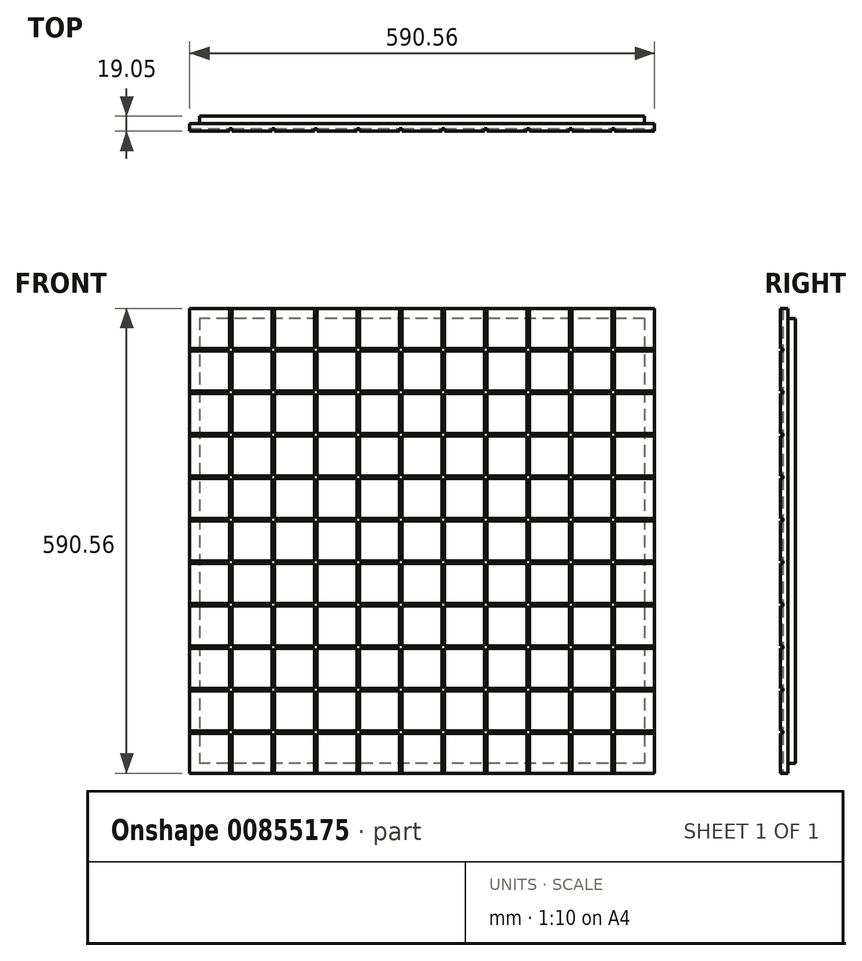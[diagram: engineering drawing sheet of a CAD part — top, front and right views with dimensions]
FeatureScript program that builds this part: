
annotation { "Feature Type Name" : "Feature", "Feature Type Description" : "" }
export const myFeature = defineFeature(function(context is Context, id is Id, definition is map)
    precondition{}
    {
        {
            var Q0;
            Q0=qCreatedBy(makeId("Front.planeOp"),FACE);
            var sketch = newSketch(context, id + "F0", { "sketchPlane" : qUnion([Q0])});
            skLineSegment(sketch, "E0.bottom", {"start": v(295.27, 295.28) * mm, "end": v(-295.27, 295.28) * mm});
            skLineSegment(sketch, "E0.top", {"start": v(295.27, -295.28) * mm, "end": v(-295.27, -295.28) * mm});
            skLineSegment(sketch, "E0.left", {"start": v(295.28, 295.27) * mm, "end": v(295.28, -295.28) * mm});
            skLineSegment(sketch, "E0.right", {"start": v(-295.28, 295.27) * mm, "end": v(-295.28, -295.27) * mm});
            skPoint(sketch, "E0.middle", {"position": v(0, 0) * mm});
            skSolve(sketch);
        }
        {
            var Q0;
            Q0=makeQuery(id+"F0.imprint","IMPRINT",FACE,{"disambiguationData":[TD([[makeQuery(id+"F0.imprint","IMPRINT",EDGE,{"derivedFrom":sQuery(id+"F0.wireOp",EDGE,"E0.bottom")}),1.0]])]});
            extrude(context, id + "F1", {"entities" : qUnion([Q0]), "depth" : 19.05 * mm, "offsetDistance" : 25.4 * mm});
        }
        {
            var Q0;
            Q0=makeQuery(id+"F1.opExtrude","CAP_FACE",FACE,{"disambiguationData":[OSD([sQuery(id+"F0.wireOp",EDGE,"E0.bottom"),sQuery(id+"F0.wireOp",EDGE,"E0.top"),sQuery(id+"F0.wireOp",EDGE,"E0.left"),sQuery(id+"F0.wireOp",EDGE,"E0.right")])],"isStart":false});
            var sketch = newSketch(context, id + "F2", { "sketchPlane" : qUnion([Q0])});
            skLineSegment(sketch, "E1.bottom", {"start": v(-244.48, 295.28) * mm, "end": v(-241.3, 295.28) * mm});
            skLineSegment(sketch, "E1.top", {"start": v(-244.47, -295.28) * mm, "end": v(-241.3, -295.28) * mm});
            skLineSegment(sketch, "E1.left", {"start": v(-244.48, 295.28) * mm, "end": v(-244.47, -295.28) * mm});
            skLineSegment(sketch, "E1.right", {"start": v(-241.3, 295.28) * mm, "end": v(-241.3, -295.28) * mm});
            skLineSegment(sketch, "E2.1.0.0", {"start": v(-190.5, 295.28) * mm, "end": v(-190.5, -295.28) * mm});
            skLineSegment(sketch, "E2.1.0.1", {"start": v(-187.32, 295.28) * mm, "end": v(-187.32, -295.28) * mm});
            skLineSegment(sketch, "E2.1.0.2", {"start": v(-190.5, 295.28) * mm, "end": v(-187.32, 295.28) * mm});
            skLineSegment(sketch, "E2.2.0.0", {"start": v(-136.52, 295.28) * mm, "end": v(-136.53, -295.28) * mm});
            skLineSegment(sketch, "E2.2.0.1", {"start": v(-133.35, 295.28) * mm, "end": v(-133.35, -295.28) * mm});
            skLineSegment(sketch, "E2.2.0.2", {"start": v(-136.52, 295.28) * mm, "end": v(-133.35, 295.28) * mm});
            skLineSegment(sketch, "E2.direction1", {"start": v(-244.47, -295.28) * mm, "end": v(-190.5, -295.28) * mm, "construction": true});
            skLineSegment(sketch, "E3.1.0.0", {"start": v(-190.5, -295.28) * mm, "end": v(-187.32, -295.28) * mm});
            skLineSegment(sketch, "E3.2.0.0", {"start": v(-136.52, -295.28) * mm, "end": v(-133.35, -295.28) * mm});
            skLineSegment(sketch, "E4.0.3.0", {"start": v(-82.55, -295.28) * mm, "end": v(-79.38, -295.28) * mm});
            skLineSegment(sketch, "E4.0.4.0", {"start": v(-28.57, -295.28) * mm, "end": v(-25.4, -295.28) * mm});
            skLineSegment(sketch, "E4.0.5.0", {"start": v(25.4, -295.28) * mm, "end": v(28.57, -295.28) * mm});
            skLineSegment(sketch, "E4.0.6.0", {"start": v(79.38, -295.28) * mm, "end": v(82.55, -295.28) * mm});
            skLineSegment(sketch, "E4.0.7.0", {"start": v(133.35, -295.28) * mm, "end": v(136.52, -295.28) * mm});
            skLineSegment(sketch, "E4.0.8.0", {"start": v(187.32, -295.28) * mm, "end": v(190.5, -295.28) * mm});
            skLineSegment(sketch, "E4.0.9.0", {"start": v(241.3, -295.28) * mm, "end": v(244.47, -295.28) * mm});
            skLineSegment(sketch, "E5.0.3.0", {"start": v(-82.55, 295.28) * mm, "end": v(-82.55, -295.28) * mm});
            skLineSegment(sketch, "E5.3.3.0", {"start": v(-79.37, 295.28) * mm, "end": v(-79.37, -295.28) * mm});
            skLineSegment(sketch, "E5.6.3.0", {"start": v(-82.55, 295.28) * mm, "end": v(-79.37, 295.28) * mm});
            skLineSegment(sketch, "E5.0.4.0", {"start": v(-28.57, 295.28) * mm, "end": v(-28.57, -295.28) * mm});
            skLineSegment(sketch, "E5.3.4.0", {"start": v(-25.4, 295.28) * mm, "end": v(-25.4, -295.28) * mm});
            skLineSegment(sketch, "E5.6.4.0", {"start": v(-28.57, 295.28) * mm, "end": v(-25.4, 295.28) * mm});
            skLineSegment(sketch, "E5.0.5.0", {"start": v(25.4, 295.28) * mm, "end": v(25.4, -295.28) * mm});
            skLineSegment(sketch, "E5.3.5.0", {"start": v(28.58, 295.28) * mm, "end": v(28.58, -295.28) * mm});
            skLineSegment(sketch, "E5.6.5.0", {"start": v(25.4, 295.28) * mm, "end": v(28.58, 295.28) * mm});
            skLineSegment(sketch, "E5.0.6.0", {"start": v(79.38, 295.28) * mm, "end": v(79.38, -295.28) * mm});
            skLineSegment(sketch, "E5.3.6.0", {"start": v(82.55, 295.28) * mm, "end": v(82.55, -295.28) * mm});
            skLineSegment(sketch, "E5.6.6.0", {"start": v(79.38, 295.28) * mm, "end": v(82.55, 295.28) * mm});
            skLineSegment(sketch, "E5.0.7.0", {"start": v(133.35, 295.28) * mm, "end": v(133.35, -295.28) * mm});
            skLineSegment(sketch, "E5.3.7.0", {"start": v(136.53, 295.28) * mm, "end": v(136.53, -295.28) * mm});
            skLineSegment(sketch, "E5.6.7.0", {"start": v(133.35, 295.28) * mm, "end": v(136.53, 295.28) * mm});
            skLineSegment(sketch, "E5.0.8.0", {"start": v(187.33, 295.28) * mm, "end": v(187.33, -295.28) * mm});
            skLineSegment(sketch, "E5.3.8.0", {"start": v(190.5, 295.28) * mm, "end": v(190.5, -295.28) * mm});
            skLineSegment(sketch, "E5.6.8.0", {"start": v(187.33, 295.28) * mm, "end": v(190.5, 295.28) * mm});
            skLineSegment(sketch, "E5.0.9.0", {"start": v(241.3, 295.28) * mm, "end": v(241.3, -295.28) * mm});
            skLineSegment(sketch, "E5.3.9.0", {"start": v(244.48, 295.28) * mm, "end": v(244.48, -295.28) * mm});
            skLineSegment(sketch, "E5.6.9.0", {"start": v(241.3, 295.28) * mm, "end": v(244.48, 295.28) * mm});
            skSolve(sketch);
        }
        {
            var Q0;
            Q0 = qSketchRegion(id + "F2", true);
            extrude(context, id + "F3", {"entities" : qUnion([Q0]), "operationType" : NewBodyOperationType.REMOVE, "oppositeDirection" : true, "depth" : 3.17 * mm, "offsetDistance" : 25.4 * mm});
        }
        {
            var Q0;
            {var subQ0=sQuery(id+"F0.wireOp",EDGE,"E0.bottom");var subQ1=sQuery(id+"F0.wireOp",EDGE,"E0.right");var subQ2=sQuery(id+"F0.wireOp",EDGE,"E0.top");Q0=makeQuery(id+"F3.boolean.opBoolean","SPLIT",FACE,{"disambiguationData":[TD([makeQuery(id+"F1.opExtrude","SWEPT_FACE",FACE,{"disambiguationData":[OSD([subQ1])]})])],"derivedFrom":makeQuery(id+"F1.opExtrude","CAP_FACE",FACE,{"disambiguationData":[OSD([subQ0,subQ2,sQuery(id+"F0.wireOp",EDGE,"E0.left"),subQ1])],"isStart":false})});}
            var sketch = newSketch(context, id + "F4", { "sketchPlane" : qUnion([Q0])});
            skLineSegment(sketch, "E6.bottom", {"start": v(-295.27, 244.47) * mm, "end": v(295.28, 244.47) * mm});
            skLineSegment(sketch, "E6.top", {"start": v(-295.27, 241.3) * mm, "end": v(295.28, 241.3) * mm});
            skLineSegment(sketch, "E6.left", {"start": v(-295.28, 244.47) * mm, "end": v(-295.28, 241.3) * mm});
            skLineSegment(sketch, "E6.right", {"start": v(295.28, 244.47) * mm, "end": v(295.28, 241.3) * mm});
            skLineSegment(sketch, "E7.0.1.0", {"start": v(-295.28, 190.5) * mm, "end": v(-295.28, 187.33) * mm});
            skLineSegment(sketch, "E7.0.1.1", {"start": v(-295.27, 190.5) * mm, "end": v(295.28, 190.5) * mm});
            skLineSegment(sketch, "E7.0.1.2", {"start": v(-295.27, 187.32) * mm, "end": v(295.28, 187.32) * mm});
            skLineSegment(sketch, "E7.0.1.3", {"start": v(295.28, 190.5) * mm, "end": v(295.28, 187.32) * mm});
            skLineSegment(sketch, "E7.0.2.0", {"start": v(-295.28, 136.53) * mm, "end": v(-295.28, 133.35) * mm});
            skLineSegment(sketch, "E7.0.2.1", {"start": v(-295.27, 136.53) * mm, "end": v(295.28, 136.53) * mm});
            skLineSegment(sketch, "E7.0.2.2", {"start": v(-295.27, 133.35) * mm, "end": v(295.28, 133.35) * mm});
            skLineSegment(sketch, "E7.0.2.3", {"start": v(295.28, 136.53) * mm, "end": v(295.28, 133.35) * mm});
            skLineSegment(sketch, "E7.0.3.0", {"start": v(-295.28, 82.55) * mm, "end": v(-295.28, 79.38) * mm});
            skLineSegment(sketch, "E7.0.3.1", {"start": v(-295.27, 82.55) * mm, "end": v(295.28, 82.55) * mm});
            skLineSegment(sketch, "E7.0.3.2", {"start": v(-295.27, 79.38) * mm, "end": v(295.28, 79.38) * mm});
            skLineSegment(sketch, "E7.0.3.3", {"start": v(295.28, 82.55) * mm, "end": v(295.28, 79.38) * mm});
            skLineSegment(sketch, "E7.0.4.0", {"start": v(-295.28, 28.58) * mm, "end": v(-295.28, 25.4) * mm});
            skLineSegment(sketch, "E7.0.4.1", {"start": v(-295.27, 28.58) * mm, "end": v(295.28, 28.58) * mm});
            skLineSegment(sketch, "E7.0.4.2", {"start": v(-295.27, 25.4) * mm, "end": v(295.28, 25.4) * mm});
            skLineSegment(sketch, "E7.0.4.3", {"start": v(295.28, 28.58) * mm, "end": v(295.28, 25.4) * mm});
            skLineSegment(sketch, "E7.0.5.0", {"start": v(-295.28, -25.4) * mm, "end": v(-295.28, -28.57) * mm});
            skLineSegment(sketch, "E7.0.5.1", {"start": v(-295.27, -25.4) * mm, "end": v(295.28, -25.4) * mm});
            skLineSegment(sketch, "E7.0.5.2", {"start": v(-295.27, -28.57) * mm, "end": v(295.28, -28.57) * mm});
            skLineSegment(sketch, "E7.0.5.3", {"start": v(295.28, -25.4) * mm, "end": v(295.28, -28.57) * mm});
            skLineSegment(sketch, "E7.0.6.0", {"start": v(-295.28, -79.37) * mm, "end": v(-295.28, -82.55) * mm});
            skLineSegment(sketch, "E7.0.6.1", {"start": v(-295.27, -79.37) * mm, "end": v(295.28, -79.37) * mm});
            skLineSegment(sketch, "E7.0.6.2", {"start": v(-295.27, -82.55) * mm, "end": v(295.28, -82.55) * mm});
            skLineSegment(sketch, "E7.0.6.3", {"start": v(295.28, -79.37) * mm, "end": v(295.28, -82.55) * mm});
            skLineSegment(sketch, "E7.0.7.0", {"start": v(-295.28, -133.35) * mm, "end": v(-295.28, -136.52) * mm});
            skLineSegment(sketch, "E7.0.7.1", {"start": v(-295.27, -133.35) * mm, "end": v(295.28, -133.35) * mm});
            skLineSegment(sketch, "E7.0.7.2", {"start": v(-295.27, -136.52) * mm, "end": v(295.28, -136.52) * mm});
            skLineSegment(sketch, "E7.0.7.3", {"start": v(295.28, -133.35) * mm, "end": v(295.28, -136.52) * mm});
            skLineSegment(sketch, "E7.0.8.0", {"start": v(-295.28, -187.32) * mm, "end": v(-295.28, -190.5) * mm});
            skLineSegment(sketch, "E7.0.8.1", {"start": v(-295.27, -187.32) * mm, "end": v(295.28, -187.32) * mm});
            skLineSegment(sketch, "E7.0.8.2", {"start": v(-295.27, -190.5) * mm, "end": v(295.28, -190.5) * mm});
            skLineSegment(sketch, "E7.0.8.3", {"start": v(295.28, -187.32) * mm, "end": v(295.28, -190.5) * mm});
            skLineSegment(sketch, "E7.0.9.0", {"start": v(-295.28, -241.3) * mm, "end": v(-295.28, -244.47) * mm});
            skLineSegment(sketch, "E7.0.9.1", {"start": v(-295.27, -241.3) * mm, "end": v(295.28, -241.3) * mm});
            skLineSegment(sketch, "E7.0.9.2", {"start": v(-295.27, -244.47) * mm, "end": v(295.28, -244.47) * mm});
            skLineSegment(sketch, "E7.0.9.3", {"start": v(295.28, -241.3) * mm, "end": v(295.28, -244.47) * mm});
            skLineSegment(sketch, "E7.1.1.0", {"start": v(-295.28, 190.5) * mm, "end": v(-295.28, 187.33) * mm});
            skLineSegment(sketch, "E7.1.1.1", {"start": v(-295.27, 190.5) * mm, "end": v(295.28, 190.5) * mm});
            skLineSegment(sketch, "E7.1.1.2", {"start": v(-295.27, 187.32) * mm, "end": v(295.28, 187.32) * mm});
            skLineSegment(sketch, "E7.1.1.3", {"start": v(295.28, 190.5) * mm, "end": v(295.28, 187.32) * mm});
            skLineSegment(sketch, "E7.1.2.0", {"start": v(-295.28, 136.53) * mm, "end": v(-295.28, 133.35) * mm});
            skLineSegment(sketch, "E7.1.2.1", {"start": v(-295.27, 136.53) * mm, "end": v(295.28, 136.53) * mm});
            skLineSegment(sketch, "E7.1.2.2", {"start": v(-295.27, 133.35) * mm, "end": v(295.28, 133.35) * mm});
            skLineSegment(sketch, "E7.1.2.3", {"start": v(295.28, 136.53) * mm, "end": v(295.28, 133.35) * mm});
            skLineSegment(sketch, "E7.1.3.0", {"start": v(-295.28, 82.55) * mm, "end": v(-295.28, 79.38) * mm});
            skLineSegment(sketch, "E7.1.3.1", {"start": v(-295.27, 82.55) * mm, "end": v(295.28, 82.55) * mm});
            skLineSegment(sketch, "E7.1.3.2", {"start": v(-295.27, 79.38) * mm, "end": v(295.28, 79.38) * mm});
            skLineSegment(sketch, "E7.1.3.3", {"start": v(295.28, 82.55) * mm, "end": v(295.28, 79.38) * mm});
            skLineSegment(sketch, "E7.1.4.0", {"start": v(-295.28, 28.58) * mm, "end": v(-295.28, 25.4) * mm});
            skLineSegment(sketch, "E7.1.4.1", {"start": v(-295.27, 28.58) * mm, "end": v(295.28, 28.58) * mm});
            skLineSegment(sketch, "E7.1.4.2", {"start": v(-295.27, 25.4) * mm, "end": v(295.28, 25.4) * mm});
            skLineSegment(sketch, "E7.1.4.3", {"start": v(295.28, 28.58) * mm, "end": v(295.28, 25.4) * mm});
            skLineSegment(sketch, "E7.1.5.0", {"start": v(-295.28, -25.4) * mm, "end": v(-295.28, -28.57) * mm});
            skLineSegment(sketch, "E7.1.5.1", {"start": v(-295.27, -25.4) * mm, "end": v(295.28, -25.4) * mm});
            skLineSegment(sketch, "E7.1.5.2", {"start": v(-295.27, -28.57) * mm, "end": v(295.28, -28.57) * mm});
            skLineSegment(sketch, "E7.1.5.3", {"start": v(295.28, -25.4) * mm, "end": v(295.28, -28.57) * mm});
            skLineSegment(sketch, "E7.1.6.0", {"start": v(-295.28, -79.37) * mm, "end": v(-295.28, -82.55) * mm});
            skLineSegment(sketch, "E7.1.6.1", {"start": v(-295.27, -79.37) * mm, "end": v(295.28, -79.37) * mm});
            skLineSegment(sketch, "E7.1.6.2", {"start": v(-295.27, -82.55) * mm, "end": v(295.28, -82.55) * mm});
            skLineSegment(sketch, "E7.1.6.3", {"start": v(295.28, -79.37) * mm, "end": v(295.28, -82.55) * mm});
            skLineSegment(sketch, "E7.1.7.0", {"start": v(-295.28, -133.35) * mm, "end": v(-295.28, -136.52) * mm});
            skLineSegment(sketch, "E7.1.7.1", {"start": v(-295.27, -133.35) * mm, "end": v(295.28, -133.35) * mm});
            skLineSegment(sketch, "E7.1.7.2", {"start": v(-295.27, -136.52) * mm, "end": v(295.28, -136.52) * mm});
            skLineSegment(sketch, "E7.1.7.3", {"start": v(295.28, -133.35) * mm, "end": v(295.28, -136.52) * mm});
            skLineSegment(sketch, "E7.1.8.0", {"start": v(-295.28, -187.32) * mm, "end": v(-295.28, -190.5) * mm});
            skLineSegment(sketch, "E7.1.8.1", {"start": v(-295.27, -187.32) * mm, "end": v(295.28, -187.32) * mm});
            skLineSegment(sketch, "E7.1.8.2", {"start": v(-295.27, -190.5) * mm, "end": v(295.28, -190.5) * mm});
            skLineSegment(sketch, "E7.1.8.3", {"start": v(295.28, -187.32) * mm, "end": v(295.28, -190.5) * mm});
            skLineSegment(sketch, "E7.1.9.0", {"start": v(-295.28, -241.3) * mm, "end": v(-295.28, -244.47) * mm});
            skLineSegment(sketch, "E7.1.9.1", {"start": v(-295.27, -241.3) * mm, "end": v(295.28, -241.3) * mm});
            skLineSegment(sketch, "E7.1.9.2", {"start": v(-295.27, -244.47) * mm, "end": v(295.28, -244.47) * mm});
            skLineSegment(sketch, "E7.1.9.3", {"start": v(295.28, -241.3) * mm, "end": v(295.28, -244.47) * mm});
            skLineSegment(sketch, "E7.2.1.0", {"start": v(-295.28, 190.5) * mm, "end": v(-295.28, 187.33) * mm});
            skLineSegment(sketch, "E7.2.1.1", {"start": v(-295.27, 190.5) * mm, "end": v(295.28, 190.5) * mm});
            skLineSegment(sketch, "E7.2.1.2", {"start": v(-295.27, 187.32) * mm, "end": v(295.28, 187.32) * mm});
            skLineSegment(sketch, "E7.2.1.3", {"start": v(295.28, 190.5) * mm, "end": v(295.28, 187.32) * mm});
            skLineSegment(sketch, "E7.2.2.0", {"start": v(-295.28, 136.53) * mm, "end": v(-295.28, 133.35) * mm});
            skLineSegment(sketch, "E7.2.2.1", {"start": v(-295.27, 136.53) * mm, "end": v(295.28, 136.53) * mm});
            skLineSegment(sketch, "E7.2.2.2", {"start": v(-295.27, 133.35) * mm, "end": v(295.28, 133.35) * mm});
            skLineSegment(sketch, "E7.2.2.3", {"start": v(295.28, 136.53) * mm, "end": v(295.28, 133.35) * mm});
            skLineSegment(sketch, "E7.2.3.0", {"start": v(-295.28, 82.55) * mm, "end": v(-295.28, 79.38) * mm});
            skLineSegment(sketch, "E7.2.3.1", {"start": v(-295.27, 82.55) * mm, "end": v(295.28, 82.55) * mm});
            skLineSegment(sketch, "E7.2.3.2", {"start": v(-295.27, 79.38) * mm, "end": v(295.28, 79.38) * mm});
            skLineSegment(sketch, "E7.2.3.3", {"start": v(295.28, 82.55) * mm, "end": v(295.28, 79.38) * mm});
            skLineSegment(sketch, "E7.2.4.0", {"start": v(-295.28, 28.58) * mm, "end": v(-295.28, 25.4) * mm});
            skLineSegment(sketch, "E7.2.4.1", {"start": v(-295.27, 28.58) * mm, "end": v(295.28, 28.58) * mm});
            skLineSegment(sketch, "E7.2.4.2", {"start": v(-295.27, 25.4) * mm, "end": v(295.28, 25.4) * mm});
            skLineSegment(sketch, "E7.2.4.3", {"start": v(295.28, 28.58) * mm, "end": v(295.28, 25.4) * mm});
            skLineSegment(sketch, "E7.2.5.0", {"start": v(-295.28, -25.4) * mm, "end": v(-295.28, -28.57) * mm});
            skLineSegment(sketch, "E7.2.5.1", {"start": v(-295.27, -25.4) * mm, "end": v(295.28, -25.4) * mm});
            skLineSegment(sketch, "E7.2.5.2", {"start": v(-295.27, -28.57) * mm, "end": v(295.28, -28.57) * mm});
            skLineSegment(sketch, "E7.2.5.3", {"start": v(295.28, -25.4) * mm, "end": v(295.28, -28.57) * mm});
            skLineSegment(sketch, "E7.2.6.0", {"start": v(-295.28, -79.37) * mm, "end": v(-295.28, -82.55) * mm});
            skLineSegment(sketch, "E7.2.6.1", {"start": v(-295.27, -79.37) * mm, "end": v(295.28, -79.37) * mm});
            skLineSegment(sketch, "E7.2.6.2", {"start": v(-295.27, -82.55) * mm, "end": v(295.28, -82.55) * mm});
            skLineSegment(sketch, "E7.2.6.3", {"start": v(295.28, -79.37) * mm, "end": v(295.28, -82.55) * mm});
            skLineSegment(sketch, "E7.2.7.0", {"start": v(-295.28, -133.35) * mm, "end": v(-295.28, -136.52) * mm});
            skLineSegment(sketch, "E7.2.7.1", {"start": v(-295.27, -133.35) * mm, "end": v(295.28, -133.35) * mm});
            skLineSegment(sketch, "E7.2.7.2", {"start": v(-295.27, -136.52) * mm, "end": v(295.28, -136.52) * mm});
            skLineSegment(sketch, "E7.2.7.3", {"start": v(295.28, -133.35) * mm, "end": v(295.28, -136.52) * mm});
            skLineSegment(sketch, "E7.2.8.0", {"start": v(-295.28, -187.32) * mm, "end": v(-295.28, -190.5) * mm});
            skLineSegment(sketch, "E7.2.8.1", {"start": v(-295.27, -187.32) * mm, "end": v(295.28, -187.32) * mm});
            skLineSegment(sketch, "E7.2.8.2", {"start": v(-295.27, -190.5) * mm, "end": v(295.28, -190.5) * mm});
            skLineSegment(sketch, "E7.2.8.3", {"start": v(295.28, -187.32) * mm, "end": v(295.28, -190.5) * mm});
            skLineSegment(sketch, "E7.2.9.0", {"start": v(-295.28, -241.3) * mm, "end": v(-295.28, -244.47) * mm});
            skLineSegment(sketch, "E7.2.9.1", {"start": v(-295.27, -241.3) * mm, "end": v(295.28, -241.3) * mm});
            skLineSegment(sketch, "E7.2.9.2", {"start": v(-295.27, -244.47) * mm, "end": v(295.28, -244.47) * mm});
            skLineSegment(sketch, "E7.2.9.3", {"start": v(295.28, -241.3) * mm, "end": v(295.28, -244.47) * mm});
            skLineSegment(sketch, "E7.direction1", {"start": v(-295.28, 241.3) * mm, "end": v(-295.28, 241.3) * mm});
            skLineSegment(sketch, "E7.direction2", {"start": v(-295.28, 241.3) * mm, "end": v(-295.28, 187.33) * mm, "construction": true});
            skSolve(sketch);
        }
        {
            var Q0;
            Q0 = qSketchRegion(id + "F4", true);
            extrude(context, id + "F5", {"entities" : qUnion([Q0]), "operationType" : NewBodyOperationType.REMOVE, "oppositeDirection" : true, "depth" : 3.17 * mm, "offsetDistance" : 25.4 * mm});
        }
        {
            var Q0;
            Q0=makeQuery(id+"F1.opExtrude","CAP_FACE",FACE,{"disambiguationData":[OSD([sQuery(id+"F0.wireOp",EDGE,"E0.bottom"),sQuery(id+"F0.wireOp",EDGE,"E0.top"),sQuery(id+"F0.wireOp",EDGE,"E0.left"),sQuery(id+"F0.wireOp",EDGE,"E0.right")])],"isStart":true});
            var sketch = newSketch(context, id + "F6", { "sketchPlane" : qUnion([Q0])});
            skLineSegment(sketch, "E8.0", {"start": v(282.58, 282.58) * mm, "end": v(282.58, -282.58) * mm});
            skLineSegment(sketch, "E8.1", {"start": v(-282.58, 282.58) * mm, "end": v(282.58, 282.58) * mm});
            skLineSegment(sketch, "E8.2", {"start": v(-282.58, 282.57) * mm, "end": v(-282.58, -282.58) * mm});
            skLineSegment(sketch, "E8.3", {"start": v(-282.58, -282.58) * mm, "end": v(282.58, -282.58) * mm});
            skLineSegment(sketch, "E9.0", {"start": v(295.28, 295.28) * mm, "end": v(295.28, -295.27) * mm});
            skLineSegment(sketch, "E10.0", {"start": v(-295.28, -295.28) * mm, "end": v(295.28, -295.28) * mm});
            skLineSegment(sketch, "E11.0", {"start": v(-295.28, 295.28) * mm, "end": v(-295.28, -295.28) * mm});
            skLineSegment(sketch, "E12.0", {"start": v(-295.27, 295.28) * mm, "end": v(295.27, 295.28) * mm});
            skSolve(sketch);
        }
        {
            var Q0;
            Q0 = qSketchRegion(id + "F6", true);
            extrude(context, id + "F7", {"entities" : qUnion([Q0]), "operationType" : NewBodyOperationType.REMOVE, "oppositeDirection" : true, "depth" : 9.52 * mm, "offsetDistance" : 25.4 * mm});
        }
    });
